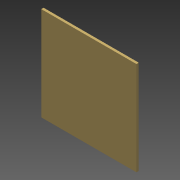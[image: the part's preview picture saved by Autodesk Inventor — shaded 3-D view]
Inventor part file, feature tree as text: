
AUTODESK INVENTOR PART (.ipt)
format: ipt  version: 2014 SP2 (Build 180246200, 246)  size: 80,896 bytes
history: native  units: mm
features: other x1, extrude x1, sketch x1
ambient origin geometry x8: Origin, YZ Plane, XZ Plane, XY Plane, X Axis, Y Axis, Z Axis, Center Point
bodies: Body1 (feature_tree)
feature tree (3):
  other  "Bryła1"
  extrude  "Wyciągnięcie proste1"  Depth=405.0mm
  sketch  "Szkic1"
